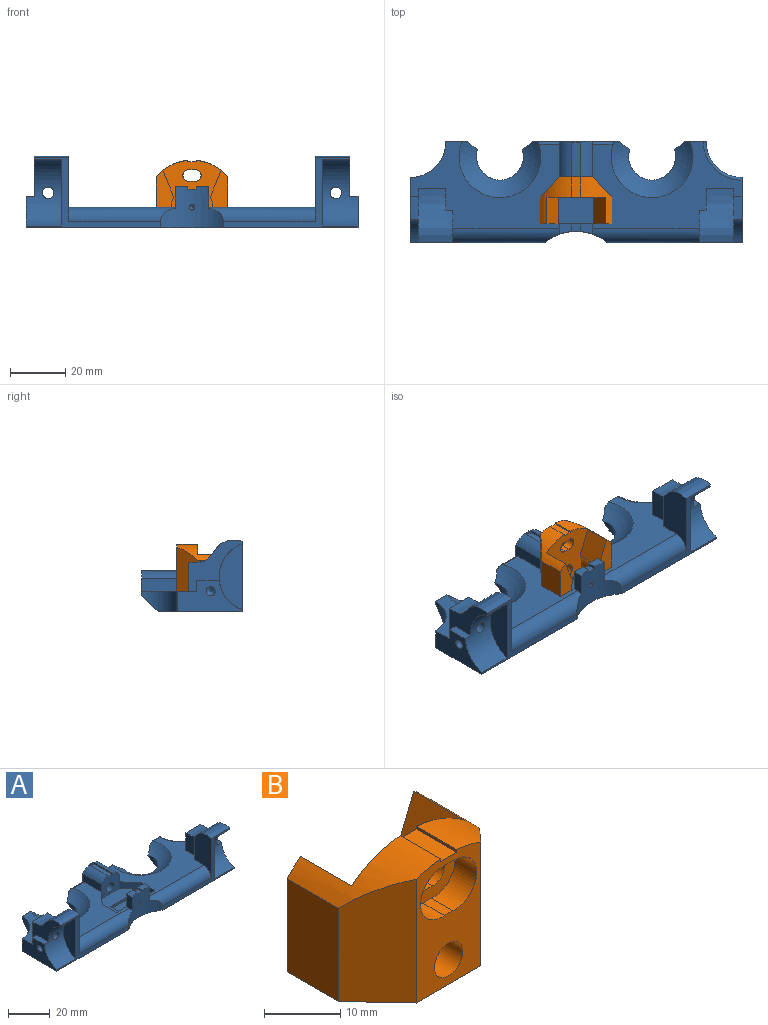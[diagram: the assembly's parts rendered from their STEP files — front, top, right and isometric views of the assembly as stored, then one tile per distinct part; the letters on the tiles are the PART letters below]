
ASSEMBLY  parts=2 mates=1
PART A: 85 faces, bbox 120.1x37.3x26.2 mm
  f0: cylinder r=18mm len=22.63mm, axis (0,0,1), area 250.2mm2, adj f6,f10,f18,f20,f36,f37,f38,f46
  f1: plane 10.41x10mm, normal (0,1,0), area 59.9mm2, adj f12,f26,f59,f64,f77
  f2: plane 10.41x10mm, normal (0,1,0), area 59.9mm2, adj f3,f11,f25,f61,f74
  f3: extruded ~19.5x12.5mm, area 260.2mm2, adj f2,f6,f11,f13,f74,f75
  f4: plane 7.7x1.56mm, normal (0,1,0), area 9.8mm2, adj f19,f25,f58,f73,f80
  f5: plane 23.5x11.5mm, normal (1,0,0), area 169.5mm2, adj f6,f7,f18,f25,f29,f67,f68,f73
  f6: plane 48.69x25.52mm, normal (0,-1,0), area 164.5mm2, adj f0,f3,f5,f11,f13,f18,f68,f69
  f7: plane 8.07x3mm, normal (0,0,1), area 24.2mm2, adj f5,f11,f29,f68
  f8: cylinder r=2.1mm len=5.19mm, axis (0,-1,0), area 67.3mm2, adj f62,f68
  f9: cylinder r=12.7mm len=23.96mm, axis (-1,0,0), area 342.5mm2, adj f10,f12,f15,f28,f63,f65
  f10: plane 48.69x25.52mm, normal (0,-1,0), area 164.5mm2, adj f0,f9,f12,f14,f18,f28,f63,f64
  f11: plane 19.52x18.64mm, normal (1,0,0), area 134.5mm2, adj f2,f3,f6,f7,f25,f29,f68
  f12: plane 19.52x18.64mm, normal (-1,0,0), area 134.5mm2, adj f1,f9,f10,f15,f26,f27,f64
  f13: plane 23.56x11.54mm, normal (-1,0,0), area 203.4mm2, adj f3,f6,f25,f75,f83
  f14: plane 23.56x11.54mm, normal (1,0,0), area 203.4mm2, adj f10,f26,f64,f76,f84
  f15: plane 8.07x3mm, normal (0,0,1), area 24.2mm2, adj f9,f12,f27,f28
  f16: plane 31.28x9.01mm, normal (0,1,0), area 61.4mm2, adj f19,f21,f30,f39,f45,f53,f57,f81
  f17: plane 7.7x1.56mm, normal (0,1,0), area 10mm2, adj f26,f53,f56,f72
  f18: plane 120x30.5mm, normal (0,0,-1), area 3275.3mm2, adj f0,f5,f6,f10,f28,f54,f55,f56
  f19: sphere r=21.25mm, area 353.1mm2, adj f4,f16,f25,f54,f57,f58,f82
  f20: plane 4.5x3.78mm, normal (0,0,1), area 14.4mm2, adj f0,f33,f37,f48
  f21: plane 12.75x5.5mm, normal (1,0,0), area 57.6mm2, adj f16,f22,f25,f45,f82
  f22: plane 12x11.35mm, normal (0,-1,0), area 102.7mm2, adj f21,f23,f24,f30,f31,f35,f45,f49
  f23: plane 26x17mm, normal (0,0,1), area 247mm2, adj f22,f31,f32,f33,f34,f35,f41,f42
  f24: cylinder r=2.62mm len=6.05mm, axis (0,1,0), area 99.8mm2, adj f22,f40
  f25: plane 54x31.5mm, normal (0,0,1), area 748mm2, adj f2,f4,f5,f11,f13,f19,f21,f29
  f26: plane 54x31.5mm, normal (0,0,1), area 769.2mm2, adj f1,f12,f14,f17,f27,f28,f30,f31
  f27: plane 4x3mm, normal (0,1,0), area 12mm2, adj f12,f15,f26,f28
  f28: plane 23.5x11.5mm, normal (-1,0,0), area 169.7mm2, adj f9,f10,f15,f18,f26,f27,f71,f72
  f29: plane 4x3mm, normal (0,1,0), area 12mm2, adj f5,f7,f11,f25
  f30: plane 12.75x5.5mm, normal (-1,0,0), area 57.6mm2, adj f16,f22,f26,f45,f81
  f31: plane 7.5x7mm, normal (0.73,-0.68,0), area 41mm2, adj f22,f23,f26,f32
  f32: plane 9.5x4mm, normal (1,0,0), area 38mm2, adj f23,f26,f31,f33
  f33: plane 26x13mm, normal (0,1,0), area 213.5mm2, adj f20,f23,f25,f26,f32,f34,f36,f37
  f34: plane 9.5x4mm, normal (-1,0,0), area 38mm2, adj f23,f25,f33,f35
  f35: plane 7.5x7mm, normal (-0.73,-0.68,0), area 41mm2, adj f22,f23,f25,f34
  f36: plane 7.93x3.78mm, normal (1,0,0), area 28.6mm2, adj f0,f25,f33,f38,f83
  f37: plane 7.93x3.78mm, normal (-1,0,0), area 28.6mm2, adj f0,f20,f26,f33,f84
  f38: plane 4.5x3.78mm, normal (0,0,1), area 14.4mm2, adj f0,f33,f36,f47
  f39: cylinder r=4.5mm len=9mm, axis (0,1,0), area 167.9mm2, adj f16,f40,f57
  f40: plane 9x9mm, normal (0,1,0), area 42mm2, adj f24,f39
  f41: plane 9.5x1.5mm, normal (1,0,0), area 14.2mm2, adj f23,f33,f43,f44
  f42: plane 9.5x1.5mm, normal (-1,0,0), area 14.2mm2, adj f23,f33,f43,f44
  f43: plane 15x1.5mm, normal (0,-1,0), area 22.5mm2, adj f23,f41,f42,f44
  f44: plane 15x9.5mm, normal (0,0,1), area 142.5mm2, adj f33,f41,f42,f43
  f45: cylinder r=7.5mm len=12.75mm, axis (0,1,0), area 139.9mm2, adj f16,f21,f22,f30,f50,f51,f52
  f46: plane 3x2.81mm, normal (0,0,1), area 8.3mm2, adj f0,f33,f47,f48
  f47: plane 2.81x1mm, normal (-1,0,0), area 2.8mm2, adj f0,f33,f38,f46
  f48: plane 2.81x1mm, normal (1,0,0), area 2.8mm2, adj f0,f20,f33,f46
  f49: plane 12.39x3mm, normal (0,0,1), area 37.2mm2, adj f22,f50,f51,f52
  f50: plane 12.39x0.85mm, normal (-1,0,0), area 10.5mm2, adj f22,f45,f49,f52
  f51: plane 12.39x0.85mm, normal (1,0,0), area 10.5mm2, adj f22,f45,f49,f52
  f52: plane 3x1mm, normal (0,-1,0), area 2.8mm2, adj f45,f49,f50,f51
  f53: sphere r=21.25mm, area 353.1mm2, adj f16,f17,f26,f55,f56,f57,f81
  f54: cylinder r=8.5mm len=17mm, axis (0,0,1), area 94.9mm2, adj f18,f19,f57,f58
  f55: cylinder r=8.5mm len=17mm, axis (0,0,1), area 94.9mm2, adj f18,f53,f56,f57
  f56: plane 12.96x6.04mm, normal (0,0.71,-0.71), area 91.4mm2, adj f17,f18,f53,f55,f72
  f57: plane 38.94x6.04mm, normal (0,0.71,-0.71), area 284.3mm2, adj f16,f18,f19,f39,f53,f54,f55
  f58: plane 12.96x6.04mm, normal (0,0.71,-0.71), area 91.4mm2, adj f4,f18,f19,f54,f73
  f59: cylinder r=3.75mm len=7.5mm, axis (0,1,0), area 141.4mm2, adj f1,f60
  f60: plane 7.5x7.5mm, normal (0,1,0), area 30.3mm2, adj f59,f65
  f61: cylinder r=3.75mm len=7.5mm, axis (0,1,0), area 141.4mm2, adj f2,f62
  f62: plane 7.5x7.5mm, normal (0,1,0), area 30.3mm2, adj f8,f61
  f63: plane 23.96x8.49mm, normal (-1,0,0), area 148.4mm2, adj f9,f10
  f64: extruded ~19.5x12.5mm, area 260.2mm2, adj f1,f10,f12,f14,f76,f77
  f65: cylinder r=2.1mm len=5.19mm, axis (0,-1,0), area 67.3mm2, adj f9,f60
  f66: cone r=0mm half-angle=59deg, axis (1,0,0), area 10mm2, adj f67
  f67: cylinder r=1.65mm len=9mm, axis (1,0,0), area 93.3mm2, adj f5,f66
  f68: cylinder r=12.7mm len=23.96mm, axis (1,0,0), area 342.6mm2, adj f5,f6,f7,f8,f11,f69
  f69: plane 23.96x8.49mm, normal (1,0,0), area 148.4mm2, adj f6,f68
  f70: cone r=0mm half-angle=59deg, axis (-1,0,0), area 10mm2, adj f71
  f71: cylinder r=1.65mm len=9mm, axis (-1,0,0), area 93.3mm2, adj f28,f70
  f72: cylinder r=13mm len=13mm, axis (0,0,1), area 134.8mm2, adj f17,f18,f26,f28,f56
  f73: cylinder r=13mm len=13mm, axis (0,0,1), area 114.4mm2, adj f4,f5,f18,f58,f80
  f74: plane 13.11x8.17mm, normal (-1,0,0), area 86.8mm2, adj f2,f3,f25,f75
  f75: plane 12.97x2.5mm, normal (0,1,0), area 32.4mm2, adj f3,f13,f25,f74
  f76: plane 12.97x2.5mm, normal (0,1,0), area 32.4mm2, adj f14,f26,f64,f77
  f77: plane 13.11x8.17mm, normal (1,0,0), area 86.8mm2, adj f1,f26,f64,f76
  f78: cone r=0mm half-angle=59deg, axis (0,-1,0), area 3.7mm2, adj f79
  f79: cylinder r=1mm len=2.03mm, axis (0,-1,0), area 12.7mm2, adj f0,f78
  f80: torus R=14mm, axis (0,0,1), area 33mm2, adj f4,f5,f25,f73
  f81: cylinder r=1mm len=8.96mm, axis (-1,0,0), area 12.6mm2, adj f16,f26,f30,f53
  f82: cylinder r=1mm len=8.96mm, axis (-1,0,0), area 12.6mm2, adj f16,f19,f21,f25
  f83: cylinder r=5mm len=38.5mm, axis (1,0,0), area 280.8mm2, adj f0,f6,f13,f25,f36
  f84: cylinder r=5mm len=38.5mm, axis (1,0,0), area 280.8mm2, adj f0,f10,f14,f26,f37
PART B: 28 faces, bbox 26x17x20.9 mm
  f0: plane 26x17mm, normal (0,0,-1), area 269mm2, adj f2,f8,f9,f10,f11,f12,f15,f16
  f1: cylinder r=17mm len=17mm, axis (0,1,0), area 98.1mm2, adj f2,f8,f11,f14,f16,f25,f27
  f2: plane 20.93x12mm, normal (0,-1,0), area 155.1mm2, adj f0,f1,f3,f17,f18,f19,f20,f21
  f3: cylinder r=17mm len=17mm, axis (0,1,0), area 98.1mm2, adj f2,f9,f10,f13,f16,f24,f26
  f4: cylinder r=9.4mm len=3.5mm, axis (0,-1,0), area 6.9mm2, adj f5,f7,f16,f22
  f5: cylinder r=2.1mm len=4.19mm, axis (0,-1,0), area 23.1mm2, adj f4,f6,f16,f22
  f6: cylinder r=13.6mm len=3.5mm, axis (0,-1,0), area 10mm2, adj f5,f7,f16,f22
  f7: cylinder r=2.1mm len=4.19mm, axis (0,-1,0), area 23.1mm2, adj f4,f6,f16,f22
  f8: plane 17.36x6.66mm, normal (0,1,0), area 85mm2, adj f0,f1,f11,f14,f15
  f9: plane 17.36x6.66mm, normal (0,1,0), area 85mm2, adj f0,f3,f10,f12,f13
  f10: plane 14.95x9.5mm, normal (1,0,0), area 142.1mm2, adj f0,f3,f9,f26
  f11: plane 14.95x9.5mm, normal (-1,0,0), area 142.1mm2, adj f0,f1,f8,f27
  f12: cylinder r=7.5mm len=9.5mm, axis (0,1,0), area 75.8mm2, adj f0,f9,f13,f16
  f13: plane 9.75x9.5mm, normal (-0.93,0,0.37), area 99.9mm2, adj f3,f9,f12,f16
  f14: plane 9.75x9.5mm, normal (0.93,0,0.37), area 99.9mm2, adj f1,f8,f15,f16
  f15: cylinder r=7.5mm len=9.5mm, axis (0,1,0), area 75.8mm2, adj f0,f8,f14,f16
  f16: plane 21.04x20.93mm, normal (0,1,0), area 280.9mm2, adj f0,f1,f3,f4,f5,f6,f7,f12
  f17: cylinder r=2.62mm len=7.5mm, axis (0,-1,0), area 123.7mm2, adj f2,f16
  f18: cylinder r=15.5mm len=4mm, axis (0,-1,0), area 13mm2, adj f2,f19,f21,f22
  f19: cylinder r=4mm len=7.98mm, axis (0,-1,0), area 50.3mm2, adj f2,f18,f20,f22
  f20: cylinder r=7.5mm len=4mm, axis (0,-1,0), area 6.3mm2, adj f2,f19,f21,f22
  f21: cylinder r=4mm len=7.98mm, axis (0,-1,0), area 50.3mm2, adj f2,f18,f20,f22
  f22: plane 10.4x8.06mm, normal (0,-1,0), area 45.6mm2, adj f4,f5,f6,f7,f18,f19,f20,f21
  f23: plane 7.5x3mm, normal (0,0,1), area 22.5mm2, adj f2,f16,f24,f25
  f24: plane 7.5x0.43mm, normal (-1,0,0), area 3.3mm2, adj f2,f3,f16,f23
  f25: plane 7.5x0.43mm, normal (1,0,0), area 3.3mm2, adj f1,f2,f16,f23
  f26: plane 19.91x7.5mm, normal (0.73,-0.68,0), area 183.4mm2, adj f0,f2,f3,f10
  f27: plane 19.91x7.5mm, normal (-0.73,-0.68,0), area 183.4mm2, adj f0,f1,f2,f11
PLACE A at identity fixed
PLACE B rot(axis=(0,0,1),180deg) t=(0,0,0)mm
MATE fastened B.f0 <-> A.f23  axis (0,0,-1) through (13,-4.75,-4)mm
